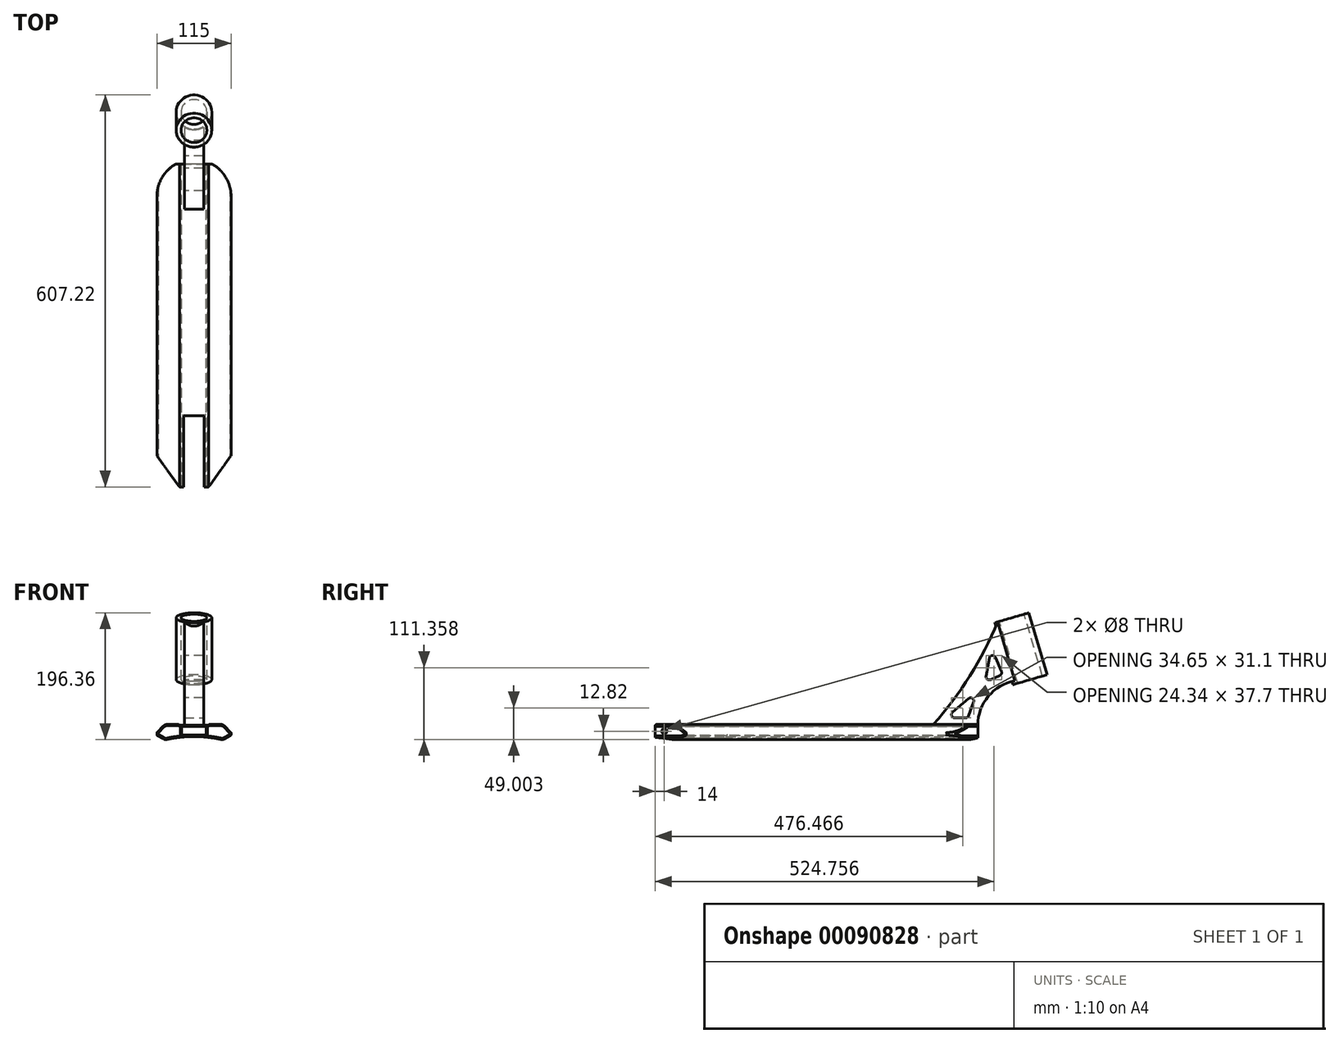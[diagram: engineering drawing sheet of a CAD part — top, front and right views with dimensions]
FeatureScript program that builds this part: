
annotation { "Feature Type Name" : "Feature", "Feature Type Description" : "" }
export const myFeature = defineFeature(function(context is Context, id is Id, definition is map)
    precondition{}
    {
        {
            var Q0;
            Q0=qCreatedBy(makeId("Front.planeOp"),FACE);
            var sketch = newSketch(context, id + "F0", { "sketchPlane" : qUnion([Q0])});
            skLineSegment(sketch, "E0", {"start": v(0, 0) * mm, "end": v(0, 70.92) * mm, "construction": true});
            skLineSegment(sketch, "E1", {"start": v(45, 12.76) * mm, "end": v(57.5, 19.98) * mm});
            skLineSegment(sketch, "E2", {"start": v(57.5, 19.98) * mm, "end": v(57.5, 23.98) * mm});
            skLineSegment(sketch, "E3", {"start": v(57.5, 23.98) * mm, "end": v(45, 36.76) * mm});
            skLineSegment(sketch, "E4", {"start": v(45, 36.76) * mm, "end": v(22.5, 36.76) * mm});
            skLineSegment(sketch, "E5", {"start": v(22.5, 36.76) * mm, "end": v(22.5, 35.46) * mm});
            skLineSegment(sketch, "E6", {"start": v(22.5, 35.46) * mm, "end": v(0, 35.46) * mm});
            skLineSegment(sketch, "E7.MirrorCS", {"start": v(-57.5, 19.98) * mm, "end": v(-57.5, 23.98) * mm});
            skLineSegment(sketch, "E8.MirrorCS", {"start": v(-22.5, 36.76) * mm, "end": v(-22.5, 35.46) * mm});
            skLineSegment(sketch, "E9.MirrorCS", {"start": v(-57.5, 23.98) * mm, "end": v(-45, 36.76) * mm});
            skLineSegment(sketch, "E10.MirrorCS", {"start": v(-45, 36.76) * mm, "end": v(-22.5, 36.76) * mm});
            skLineSegment(sketch, "E11.MirrorCS", {"start": v(-45, 12.76) * mm, "end": v(-57.5, 19.98) * mm});
            skLineSegment(sketch, "E12.MirrorCS", {"start": v(-22.5, 35.46) * mm, "end": v(0, 35.46) * mm});
            skArc(sketch, "E13", {"start": v(45, 12.76) * mm, "mid": v(0, 17.9) * mm, "end": v(-45, 12.76) * mm});
            skSolve(sketch);
        }
        {
            var Q0;
            Q0 = qSketchRegion(id + "F0", true);
            extrude(context, id + "F1", {"entities" : qUnion([Q0]), "depth" : 500 * mm});
        }
        {
            var Q0;
            Q0=qCreatedBy(makeId("Front.planeOp"),FACE);
            var sketch = newSketch(context, id + "F2", { "sketchPlane" : qUnion([Q0])});
            skLineSegment(sketch, "E14", {"start": v(0, 0) * mm, "end": v(0, 112.07) * mm, "construction": true});
            skLineSegment(sketch, "E15.bottom", {"start": v(-19, 33.46) * mm, "end": v(19, 33.46) * mm});
            skLineSegment(sketch, "E15.top", {"start": v(-19, 20.46) * mm, "end": v(19, 20.46) * mm});
            skLineSegment(sketch, "E15.left", {"start": v(-19, 33.46) * mm, "end": v(-19, 20.46) * mm});
            skLineSegment(sketch, "E15.right", {"start": v(19, 33.46) * mm, "end": v(19, 20.46) * mm});
            skSolve(sketch);
        }
        {
            var Q0;
            Q0=makeQuery(id+"F2.imprint","IMPRINT",FACE,{"disambiguationData":[TD([[makeQuery(id+"F2.imprint","IMPRINT",EDGE,{"derivedFrom":sQuery(id+"F2.wireOp",EDGE,"E15.bottom")}),-1.0]])]});
            extrude(context, id + "F3", {"entities" : qUnion([Q0]), "operationType" : NewBodyOperationType.REMOVE, "depth" : 500 * mm});
        }
        {
            var Q0;
            Q0=makeQuery(id+"F1.opExtrude","SWEPT_EDGE",EDGE,{"disambiguationData":[OSD([sQuery(id+"F0.wireOp",EDGE,"E4"),sQuery(id+"F0.wireOp",EDGE,"E5")])]});
            var Q1;
            Q1=makeQuery(id+"F1.opExtrude","SWEPT_EDGE",EDGE,{"disambiguationData":[OSD([sQuery(id+"F0.wireOp",EDGE,"E8.MirrorCS"),sQuery(id+"F0.wireOp",EDGE,"E10.MirrorCS")])]});
            fillet(context, id + "F4", {"entities" : qUnion([Q0, Q1]), "radius" : 2 * mm, "tangentPropagation" : true, "allowEdgeOverflow" : false});
        }
        {
            var Q0;
            Q0=makeQuery(id+"F1.opExtrude","SWEPT_EDGE",EDGE,{"disambiguationData":[OSD([sQuery(id+"F0.wireOp",EDGE,"E9.MirrorCS"),sQuery(id+"F0.wireOp",EDGE,"E10.MirrorCS")])]});
            var Q1;
            Q1=makeQuery(id+"F1.opExtrude","SWEPT_EDGE",EDGE,{"disambiguationData":[OSD([sQuery(id+"F0.wireOp",EDGE,"E3"),sQuery(id+"F0.wireOp",EDGE,"E4")])]});
            var Q2;
            Q2=makeQuery(id+"F1.opExtrude","SWEPT_EDGE",EDGE,{"disambiguationData":[OSD([sQuery(id+"F0.wireOp",EDGE,"E1"),sQuery(id+"F0.wireOp",EDGE,"E13")])]});
            var Q3;
            Q3=makeQuery(id+"F1.opExtrude","SWEPT_EDGE",EDGE,{"disambiguationData":[OSD([sQuery(id+"F0.wireOp",EDGE,"E11.MirrorCS"),sQuery(id+"F0.wireOp",EDGE,"E13")])]});
            fillet(context, id + "F5", {"entities" : qUnion([Q0, Q1, Q2, Q3]), "radius" : 9 * mm, "tangentPropagation" : true, "allowEdgeOverflow" : false});
        }
        {
            var Q0;
            Q0=makeQuery(id+"F1.opExtrude","SWEPT_EDGE",EDGE,{"disambiguationData":[OSD([sQuery(id+"F0.wireOp",EDGE,"E2"),sQuery(id+"F0.wireOp",EDGE,"E3")])]});
            var Q1;
            Q1=makeQuery(id+"F1.opExtrude","SWEPT_EDGE",EDGE,{"disambiguationData":[OSD([sQuery(id+"F0.wireOp",EDGE,"E1"),sQuery(id+"F0.wireOp",EDGE,"E2")])]});
            var Q2;
            Q2=makeQuery(id+"F1.opExtrude","SWEPT_EDGE",EDGE,{"disambiguationData":[OSD([sQuery(id+"F0.wireOp",EDGE,"E7.MirrorCS"),sQuery(id+"F0.wireOp",EDGE,"E9.MirrorCS")])]});
            var Q3;
            Q3=makeQuery(id+"F1.opExtrude","SWEPT_EDGE",EDGE,{"disambiguationData":[OSD([sQuery(id+"F0.wireOp",EDGE,"E7.MirrorCS"),sQuery(id+"F0.wireOp",EDGE,"E11.MirrorCS")])]});
            fillet(context, id + "F6", {"entities" : qUnion([Q0, Q1, Q2, Q3]), "radius" : 1 * mm, "tangentPropagation" : true, "allowEdgeOverflow" : false});
        }
        {
            var Q0;
            Q0=makeQuery(id+"F1.opExtrude","CAP_FACE",FACE,{"disambiguationData":[OSD([sQuery(id+"F0.wireOp",EDGE,"E1"),sQuery(id+"F0.wireOp",EDGE,"E2"),sQuery(id+"F0.wireOp",EDGE,"E3"),sQuery(id+"F0.wireOp",EDGE,"E4"),sQuery(id+"F0.wireOp",EDGE,"E5"),sQuery(id+"F0.wireOp",EDGE,"E6"),sQuery(id+"F0.wireOp",EDGE,"E7.MirrorCS"),sQuery(id+"F0.wireOp",EDGE,"E8.MirrorCS"),sQuery(id+"F0.wireOp",EDGE,"E9.MirrorCS"),sQuery(id+"F0.wireOp",EDGE,"E10.MirrorCS"),sQuery(id+"F0.wireOp",EDGE,"E11.MirrorCS"),sQuery(id+"F0.wireOp",EDGE,"E12.MirrorCS"),sQuery(id+"F0.wireOp",EDGE,"E13")])],"isStart":false});
            var sketch = newSketch(context, id + "F7", { "sketchPlane" : qUnion([Q0])});
            skLineSegment(sketch, "E16.0", {"start": v(-57.21, 24.27) * mm, "end": v(-47.65, 34.06) * mm});
            skArc(sketch, "E17.0", {"start": v(-41.21, 36.76) * mm, "mid": v(-44.7, 36.06) * mm, "end": v(-47.65, 34.06) * mm});
            skLineSegment(sketch, "E18.0", {"start": v(-57.5, 20.56) * mm, "end": v(-57.5, 23.57) * mm});
            skArc(sketch, "E19.0", {"start": v(-57.21, 24.27) * mm, "mid": v(-57.43, 23.95) * mm, "end": v(-57.5, 23.57) * mm});
            skArc(sketch, "E20.0", {"start": v(-57.5, 20.56) * mm, "mid": v(-57.37, 20.06) * mm, "end": v(-57, 19.7) * mm});
            skLineSegment(sketch, "E21.0", {"start": v(-41.21, 36.76) * mm, "end": v(-24.37, 36.76) * mm});
            skArc(sketch, "E22.0", {"start": v(57.5, 23.57) * mm, "mid": v(57.43, 23.95) * mm, "end": v(57.21, 24.27) * mm});
            skArc(sketch, "E23.0", {"start": v(57, 19.7) * mm, "mid": v(57.37, 20.06) * mm, "end": v(57.5, 20.56) * mm});
            skLineSegment(sketch, "E24.0", {"start": v(57.5, 20.56) * mm, "end": v(57.5, 23.57) * mm});
            skLineSegment(sketch, "E25.0", {"start": v(57.21, 24.27) * mm, "end": v(47.65, 34.06) * mm});
            skLineSegment(sketch, "E26.0", {"start": v(48.03, 14.51) * mm, "end": v(57, 19.7) * mm});
            skArc(sketch, "E27.0", {"start": v(41.66, 13.5) * mm, "mid": v(44.94, 13.42) * mm, "end": v(48.03, 14.51) * mm});
            skArc(sketch, "E28.0", {"start": v(41.66, 13.5) * mm, "mid": v(0, 17.9) * mm, "end": v(-41.66, 13.5) * mm});
            skArc(sketch, "E29.0", {"start": v(47.65, 34.06) * mm, "mid": v(44.7, 36.06) * mm, "end": v(41.21, 36.76) * mm});
            skLineSegment(sketch, "E30.0", {"start": v(41.21, 36.76) * mm, "end": v(24.37, 36.76) * mm});
            skLineSegment(sketch, "E31.0", {"start": v(22.5, 35.46) * mm, "end": v(-22.5, 35.46) * mm});
            skLineSegment(sketch, "E32.0", {"start": v(-47.03, 16.25) * mm, "end": v(-55, 20.85) * mm});
            skArc(sketch, "E33.0", {"start": v(-56.89, 20.56) * mm, "mid": v(-56.83, 20.36) * mm, "end": v(-56.7, 20.22) * mm});
            skLineSegment(sketch, "E34.0", {"start": v(-55.5, 21.71) * mm, "end": v(-55.5, 22.76) * mm});
            skLineSegment(sketch, "E35.0", {"start": v(-55.21, 23.46) * mm, "end": v(-46.22, 32.66) * mm});
            skPoint(sketch, "E36.visualSharp", {"position": v(-55.5, 23.16) * mm});
            skArc(sketch, "E36.filletArc", {"start": v(-55.21, 23.46) * mm, "mid": v(-55.43, 23.13) * mm, "end": v(-55.5, 22.76) * mm});
            skPoint(sketch, "E37.visualSharp", {"position": v(-55.5, 21.13) * mm});
            skArc(sketch, "E37.filletArc", {"start": v(-55.5, 21.71) * mm, "mid": v(-55.37, 21.21) * mm, "end": v(-55, 20.85) * mm});
            skArc(sketch, "E38.0", {"start": v(-41.21, 34.76) * mm, "mid": v(-43.93, 34.22) * mm, "end": v(-46.22, 32.66) * mm});
            skArc(sketch, "E39.0", {"start": v(-47.03, 16.25) * mm, "mid": v(-44.63, 15.4) * mm, "end": v(-42.07, 15.46) * mm});
            skArc(sketch, "E40.0", {"start": v(42.07, 15.46) * mm, "mid": v(31.58, 17.4) * mm, "end": v(21, 18.8) * mm});
            skArc(sketch, "E41.0", {"start": v(42.07, 15.46) * mm, "mid": v(44.63, 15.4) * mm, "end": v(47.03, 16.25) * mm});
            skLineSegment(sketch, "E42.0", {"start": v(47.03, 16.25) * mm, "end": v(55, 20.85) * mm});
            skLineSegment(sketch, "E43.0", {"start": v(55.21, 23.46) * mm, "end": v(46.22, 32.66) * mm});
            skLineSegment(sketch, "E44.0", {"start": v(55.5, 21.71) * mm, "end": v(55.5, 22.76) * mm});
            skPoint(sketch, "E45.visualSharp", {"position": v(55.5, 21.13) * mm});
            skArc(sketch, "E45.filletArc", {"start": v(55, 20.85) * mm, "mid": v(55.37, 21.21) * mm, "end": v(55.5, 21.71) * mm});
            skPoint(sketch, "E46.visualSharp", {"position": v(55.5, 23.16) * mm});
            skArc(sketch, "E46.filletArc", {"start": v(55.5, 22.76) * mm, "mid": v(55.43, 23.13) * mm, "end": v(55.21, 23.46) * mm});
            skArc(sketch, "E47.0", {"start": v(46.22, 32.66) * mm, "mid": v(43.93, 34.22) * mm, "end": v(41.21, 34.76) * mm});
            skLineSegment(sketch, "E48", {"start": v(-21, 33.46) * mm, "end": v(-22.5, 33.46) * mm});
            skLineSegment(sketch, "E49", {"start": v(-41.21, 34.76) * mm, "end": v(-24.37, 34.76) * mm});
            skArc(sketch, "E50", {"start": v(-22.5, 33.46) * mm, "mid": v(-23.23, 34.4) * mm, "end": v(-24.37, 34.76) * mm});
            skLineSegment(sketch, "E51", {"start": v(-21, 33.46) * mm, "end": v(-21, 18.8) * mm});
            skLineSegment(sketch, "E52.0", {"start": v(41.21, 34.76) * mm, "end": v(24.37, 34.76) * mm});
            skLineSegment(sketch, "E53", {"start": v(21, 33.46) * mm, "end": v(22.5, 33.46) * mm});
            skArc(sketch, "E54", {"start": v(24.37, 34.76) * mm, "mid": v(23.23, 34.4) * mm, "end": v(22.5, 33.46) * mm});
            skLineSegment(sketch, "E55", {"start": v(21, 33.46) * mm, "end": v(21, 18.8) * mm});
            skArc(sketch, "E56.trimOffspring", {"start": v(-21, 18.8) * mm, "mid": v(-31.58, 17.4) * mm, "end": v(-42.07, 15.46) * mm});
            skSolve(sketch);
        }
        {
            var Q0;
            Q0=makeQuery(id+"F7.imprint","IMPRINT",FACE,{"disambiguationData":[TD([[makeQuery(id+"F7.imprint","IMPRINT",EDGE,{"derivedFrom":sQuery(id+"F7.wireOp",EDGE,"E40.0")}),-1.0]])]});
            var Q1;
            Q1=makeQuery(id+"F7.imprint","IMPRINT",FACE,{"disambiguationData":[TD([[makeQuery(id+"F7.imprint","IMPRINT",EDGE,{"derivedFrom":sQuery(id+"F7.wireOp",EDGE,"E32.0")}),-1.0]])]});
            extrude(context, id + "F8", {"entities" : qUnion([Q0, Q1]), "operationType" : NewBodyOperationType.REMOVE, "oppositeDirection" : true, "depth" : 500 * mm});
        }
        {
            var Q0;
            Q0=qCreatedBy(makeId("Top.planeOp"),FACE);
            var sketch = newSketch(context, id + "F9", { "sketchPlane" : qUnion([Q0])});
            skArc(sketch, "E57", {"start": v(57.5, -50) * mm, "mid": v(0, 7.5) * mm, "end": v(-57.5, -50) * mm});
            skLineSegment(sketch, "E58", {"start": v(-57.5, -50) * mm, "end": v(-57.5, 30) * mm});
            skLineSegment(sketch, "E59", {"start": v(57.5, -50) * mm, "end": v(57.5, 30) * mm});
            skLineSegment(sketch, "E60", {"start": v(57.5, 30) * mm, "end": v(-57.5, 30) * mm});
            skSolve(sketch);
        }
        {
            var Q0;
            Q0 = qSketchRegion(id + "F9", true);
            extrude(context, id + "F10", {"entities" : qUnion([Q0]), "operationType" : NewBodyOperationType.REMOVE, "depth" : 174.35 * mm});
        }
        {
            var Q0;
            Q0=qCreatedBy(makeId("Top.planeOp"),FACE);
            var sketch = newSketch(context, id + "F11", { "sketchPlane" : qUnion([Q0])});
            skLineSegment(sketch, "E61", {"start": v(57.21, -543.3) * mm, "end": v(57.21, -443.3) * mm});
            skLineSegment(sketch, "E62", {"start": v(39.1, -500) * mm, "end": v(16, -500) * mm});
            skLineSegment(sketch, "E63", {"start": v(16, -500) * mm, "end": v(16, -390) * mm});
            skLineSegment(sketch, "E64", {"start": v(16, -390) * mm, "end": v(-16, -390) * mm});
            skLineSegment(sketch, "E65", {"start": v(-16, -390) * mm, "end": v(-16, -500) * mm});
            skLineSegment(sketch, "E66", {"start": v(-16, -500) * mm, "end": v(-34.18, -500) * mm});
            skLineSegment(sketch, "E67", {"start": v(-57.21, -443.3) * mm, "end": v(-57.21, -543.3) * mm});
            skLineSegment(sketch, "E68", {"start": v(-57.21, -543.3) * mm, "end": v(57.21, -543.3) * mm});
            skLineSegment(sketch, "E69", {"start": v(57.21, -506.22) * mm, "end": v(68, -506.22) * mm});
            skLineSegment(sketch, "E70", {"start": v(68, -506.22) * mm, "end": v(68, -452.22) * mm});
            skLineSegment(sketch, "E71", {"start": v(68, -452.22) * mm, "end": v(57.21, -452.22) * mm});
            skLineSegment(sketch, "E72", {"start": v(57.21, -452.22) * mm, "end": v(57.21, -506.22) * mm});
            skLineSegment(sketch, "E73", {"start": v(-57.21, -506.22) * mm, "end": v(-68, -506.22) * mm});
            skLineSegment(sketch, "E74", {"start": v(-68, -506.22) * mm, "end": v(-68, -452.22) * mm});
            skLineSegment(sketch, "E75", {"start": v(-68, -452.22) * mm, "end": v(-57.21, -452.22) * mm});
            skLineSegment(sketch, "E76", {"start": v(-57.21, -452.22) * mm, "end": v(-57.21, -506.22) * mm});
            skLineSegment(sketch, "E77.0", {"start": v(22.5, -500) * mm, "end": v(22.5, 0) * mm});
            skLineSegment(sketch, "E78.0", {"start": v(-22.5, -500) * mm, "end": v(-22.5, 0) * mm});
            skLineSegment(sketch, "E79", {"start": v(57.21, -452.22) * mm, "end": v(22.5, -500) * mm});
            skLineSegment(sketch, "E80", {"start": v(-57.21, -452.22) * mm, "end": v(-22.5, -500) * mm});
            skSolve(sketch);
        }
        {
            var Q0;
            Q0 = qSketchRegion(id + "F11", true);
            extrude(context, id + "F12", {"entities" : qUnion([Q0]), "operationType" : NewBodyOperationType.REMOVE, "depth" : 74.4 * mm});
        }
        {
            var Q0;
            Q0=qCreatedBy(makeId("Right.planeOp"),FACE);
            var sketch = newSketch(context, id + "F13", { "sketchPlane" : qUnion([Q0])});
            skLineSegment(sketch, "E81", {"start": v(0, 35.46) * mm, "end": v(-70, 35.46) * mm});
            skArc(sketch, "E82", {"start": v(-70, 35.46) * mm, "mid": v(-12.76, 111.1) * mm, "end": v(30.63, 195.46) * mm});
            skLineSegment(sketch, "E83", {"start": v(58.76, 99.5) * mm, "end": v(58.3, 104.48) * mm});
            skArc(sketch, "E84", {"start": v(58.3, 104.48) * mm, "mid": v(16.53, 80.64) * mm, "end": v(0, 35.46) * mm});
            skLineSegment(sketch, "E85", {"start": v(30.63, 195.46) * mm, "end": v(74.78, 208.4) * mm});
            skLineSegment(sketch, "E86", {"start": v(74.78, 208.4) * mm, "end": v(102.9, 112.44) * mm});
            skLineSegment(sketch, "E87", {"start": v(58.76, 99.5) * mm, "end": v(102.9, 112.44) * mm});
            skPoint(sketch, "E88.orphan", {"position": v(106.7, 99.5) * mm});
            skSolve(sketch);
        }
        {
            var Q0;
            Q0=makeQuery(id+"F13.imprint","IMPRINT",FACE,{"disambiguationData":[TD([[makeQuery(id+"F13.imprint","IMPRINT",EDGE,{"derivedFrom":sQuery(id+"F13.wireOp",EDGE,"E81")}),-1.0]])]});
            extrude(context, id + "F14", {"entities" : qUnion([Q0]), "operationType" : NewBodyOperationType.ADD, "endBound" : BoundingType.SYMMETRIC, "depth" : 30 * mm});
        }
        {
            var Q0;
            Q0=makeQuery(id+"F14.opExtrude","SWEPT_FACE",FACE,{"disambiguationData":[OSD([sQuery(id+"F13.wireOp",EDGE,"E85")])]});
            var sketch = newSketch(context, id + "F15", { "sketchPlane" : qUnion([Q0])});
            skCircle(sketch, "E89", {"center": v(0, 107.37) * mm, "radius": 27.5 * mm});
            skPoint(sketch, "E89.centerSnap0", {"position": v(15, 107.37) * mm});
            skPoint(sketch, "E89.centerSnap1", {"position": v(0, 130.37) * mm});
            skSolve(sketch);
        }
        {
            var Q0;
            {var subQ0=sQuery(id+"F15.wireOp",EDGE,"E89");var subQ1=makeQuery(id+"F14.opExtrude","SWEPT_EDGE",EDGE,{"disambiguationData":[OSD([sQuery(id+"F13.wireOp",EDGE,"E85"),sQuery(id+"F13.wireOp",EDGE,"E86")])]});var subQ2=makeQuery(id+"F15.imprint","INTERSECT",VERTEX,{"disambiguationData":[OD(0.0)],"derivedFrom":[subQ1,subQ0]});Q0=makeQuery(id+"F15.imprint","IMPRINT",FACE,{"disambiguationData":[TD([[makeQuery(id+"F15.imprint","IMPRINT",EDGE,{"disambiguationData":[TD([[subQ2,-1.0]])],"derivedFrom":subQ0}),1.0]])]});}
            var Q1;
            {var subQ0=sQuery(id+"F15.wireOp",EDGE,"E89");var subQ1=makeQuery(id+"F14.opExtrude","CAP_EDGE",EDGE,{"disambiguationData":[OSD([sQuery(id+"F13.wireOp",EDGE,"E85")])],"isStart":false});var subQ2=makeQuery(id+"F15.imprint","INTERSECT",VERTEX,{"disambiguationData":[OD(0.0)],"derivedFrom":[subQ1,subQ0]});Q1=makeQuery(id+"F15.imprint","IMPRINT",FACE,{"disambiguationData":[TD([[makeQuery(id+"F15.imprint","IMPRINT",EDGE,{"disambiguationData":[TD([[subQ2,1.0]])],"derivedFrom":subQ0}),1.0]])]});}
            var Q2;
            {var subQ0=sQuery(id+"F15.wireOp",EDGE,"E89");var subQ1=makeQuery(id+"F14.opExtrude","CAP_EDGE",EDGE,{"disambiguationData":[OSD([sQuery(id+"F13.wireOp",EDGE,"E85")])],"isStart":true});var subQ2=makeQuery(id+"F15.imprint","INTERSECT",VERTEX,{"disambiguationData":[OD(0.0)],"derivedFrom":[subQ1,subQ0]});Q2=makeQuery(id+"F15.imprint","IMPRINT",FACE,{"disambiguationData":[TD([[makeQuery(id+"F15.imprint","IMPRINT",EDGE,{"disambiguationData":[TD([[subQ2,-1.0]])],"derivedFrom":subQ0}),1.0]])]});}
            var Q3;
            {var subQ0=sQuery(id+"F15.wireOp",EDGE,"E89");var subQ1=sQuery(id+"F13.wireOp",EDGE,"E85");var subQ8=makeQuery(id+"F14.opExtrude","CAP_EDGE",EDGE,{"disambiguationData":[OSD([subQ1])],"isStart":true});var subQ9=makeQuery(id+"F15.imprint","INTERSECT",VERTEX,{"disambiguationData":[OD(0.0)],"derivedFrom":[subQ8,subQ0]});Q3=makeQuery(id+"F15.imprint","IMPRINT",FACE,{"disambiguationData":[TD([[makeQuery(id+"F15.imprint","IMPRINT",EDGE,{"disambiguationData":[TD([[subQ9,1.0]])],"derivedFrom":subQ8}),-1.0]])]});}
            var Q4;
            {var subQ0=sQuery(id+"F15.wireOp",EDGE,"E89");var subQ1=makeQuery(id+"F14.opExtrude","SWEPT_EDGE",EDGE,{"disambiguationData":[OSD([sQuery(id+"F13.wireOp",EDGE,"E82"),sQuery(id+"F13.wireOp",EDGE,"E85")])]});var subQ2=makeQuery(id+"F15.imprint","INTERSECT",VERTEX,{"disambiguationData":[OD(0.0)],"derivedFrom":[subQ1,subQ0]});Q4=makeQuery(id+"F15.imprint","IMPRINT",FACE,{"disambiguationData":[TD([[makeQuery(id+"F15.imprint","IMPRINT",EDGE,{"disambiguationData":[TD([[subQ2,-1.0]])],"derivedFrom":subQ0}),1.0]])]});}
            var Q5;
            Q5=makeQuery(id+"F14.opExtrude","SWEPT_FACE",FACE,{"disambiguationData":[OSD([sQuery(id+"F13.wireOp",EDGE,"E87")])]});
            extrude(context, id + "F16", {"entities" : qUnion([Q0, Q1, Q2, Q3, Q4]), "operationType" : NewBodyOperationType.ADD, "endBound" : BoundingType.UP_TO_SURFACE, "oppositeDirection" : true, "endBoundEntityFace" : qUnion([Q5]), "depth" : 125.58 * mm});
        }
        {
            var Q0;
            Q0=sQuery(id+"F15.wireOp",VERTEX,"E89.center");
            var Q1;
            Q1=makeQuery(id+"F1.opExtrude","SWEPT_BODY",BODY,{"disambiguationData":[OSD([sQuery(id+"F0.wireOp",EDGE,"E1"),sQuery(id+"F0.wireOp",EDGE,"E2"),sQuery(id+"F0.wireOp",EDGE,"E3"),sQuery(id+"F0.wireOp",EDGE,"E4"),sQuery(id+"F0.wireOp",EDGE,"E5"),sQuery(id+"F0.wireOp",EDGE,"E6"),sQuery(id+"F0.wireOp",EDGE,"E7.MirrorCS"),sQuery(id+"F0.wireOp",EDGE,"E8.MirrorCS"),sQuery(id+"F0.wireOp",EDGE,"E9.MirrorCS"),sQuery(id+"F0.wireOp",EDGE,"E10.MirrorCS"),sQuery(id+"F0.wireOp",EDGE,"E11.MirrorCS"),sQuery(id+"F0.wireOp",EDGE,"E12.MirrorCS"),sQuery(id+"F0.wireOp",EDGE,"E13")])]});
            hole(context, id + "F17", {"style" : HoleStyle.SIMPLE, "endStyle" : HoleEndStyle.THROUGH, "holeDiameter" : 40 * mm, "locations" : qUnion([Q0]), "scope" : qUnion([Q1]), "isTappedThrough" : true});
        }
        {
            var Q0;
            Q0=makeQuery(id+"F8.boolean.opBoolean","COPY",FACE,{"derivedFrom":makeQuery(id+"F8.opExtrude","SWEPT_FACE",FACE,{"disambiguationData":[OSD([sQuery(id+"F7.wireOp",EDGE,"E55")])]})});
            var sketch = newSketch(context, id + "F18", { "sketchPlane" : qUnion([Q0])});
            skPoint(sketch, "E90", {"position": v(-486, 26.13) * mm});
            skPoint(sketch, "E90.positionSnap0", {"position": v(-500, 26.13) * mm});
            skSolve(sketch);
        }
        {
            var Q0;
            Q0=sQuery(id+"F18.wireOp",VERTEX,"E90");
            var Q1;
            Q1=makeQuery(id+"F1.opExtrude","SWEPT_BODY",BODY,{"disambiguationData":[OSD([sQuery(id+"F0.wireOp",EDGE,"E1"),sQuery(id+"F0.wireOp",EDGE,"E2"),sQuery(id+"F0.wireOp",EDGE,"E3"),sQuery(id+"F0.wireOp",EDGE,"E4"),sQuery(id+"F0.wireOp",EDGE,"E5"),sQuery(id+"F0.wireOp",EDGE,"E6"),sQuery(id+"F0.wireOp",EDGE,"E7.MirrorCS"),sQuery(id+"F0.wireOp",EDGE,"E8.MirrorCS"),sQuery(id+"F0.wireOp",EDGE,"E9.MirrorCS"),sQuery(id+"F0.wireOp",EDGE,"E10.MirrorCS"),sQuery(id+"F0.wireOp",EDGE,"E11.MirrorCS"),sQuery(id+"F0.wireOp",EDGE,"E12.MirrorCS"),sQuery(id+"F0.wireOp",EDGE,"E13")])]});
            hole(context, id + "F19", {"style" : HoleStyle.SIMPLE, "endStyle" : HoleEndStyle.THROUGH, "holeDiameter" : 8 * mm, "locations" : qUnion([Q0]), "scope" : qUnion([Q1]), "isTappedThrough" : true});
        }
        {
            var Q0;
            Q0=makeQuery(id+"F14.opExtrude","CAP_FACE",FACE,{"disambiguationData":[OSD([sQuery(id+"F13.wireOp",EDGE,"E81"),sQuery(id+"F13.wireOp",EDGE,"E82"),sQuery(id+"F13.wireOp",EDGE,"E83"),sQuery(id+"F13.wireOp",EDGE,"E84"),sQuery(id+"F13.wireOp",EDGE,"E85"),sQuery(id+"F13.wireOp",EDGE,"E86"),sQuery(id+"F13.wireOp",EDGE,"E87")])],"isStart":false});
            var sketch = newSketch(context, id + "F20", { "sketchPlane" : qUnion([Q0])});
            skLineSegment(sketch, "E91", {"start": v(-49.4, 46.76) * mm, "end": v(-15.4, 46.76) * mm});
            skLineSegment(sketch, "E92", {"start": v(-15.4, 46.76) * mm, "end": v(0, 89.05) * mm});
            skLineSegment(sketch, "E93", {"start": v(0, 89.05) * mm, "end": v(-49.4, 46.76) * mm});
            skLineSegment(sketch, "E94", {"start": v(20.6, 155.7) * mm, "end": v(10.98, 102.47) * mm});
            skLineSegment(sketch, "E95", {"start": v(10.98, 102.47) * mm, "end": v(38.5, 114.4) * mm});
            skLineSegment(sketch, "E96", {"start": v(38.5, 114.4) * mm, "end": v(20.6, 155.7) * mm});
            skSolve(sketch);
        }
        {
            var Q0;
            Q0 = qSketchRegion(id + "F20", true);
            extrude(context, id + "F21", {"entities" : qUnion([Q0]), "operationType" : NewBodyOperationType.REMOVE, "oppositeDirection" : true, "depth" : 55 * mm});
        }
        {
            var Q0;
            Q0=makeQuery(id+"F21.boolean.opBoolean","COPY",EDGE,{"derivedFrom":makeQuery(id+"F21.opExtrude","SWEPT_EDGE",EDGE,{"disambiguationData":[OSD([sQuery(id+"F20.wireOp",EDGE,"E95"),sQuery(id+"F20.wireOp",EDGE,"E96")])]})});
            var Q1;
            Q1=makeQuery(id+"F21.boolean.opBoolean","COPY",EDGE,{"derivedFrom":makeQuery(id+"F21.opExtrude","SWEPT_EDGE",EDGE,{"disambiguationData":[OSD([sQuery(id+"F20.wireOp",EDGE,"E94"),sQuery(id+"F20.wireOp",EDGE,"E95")])]})});
            var Q2;
            Q2=makeQuery(id+"F21.boolean.opBoolean","COPY",EDGE,{"derivedFrom":makeQuery(id+"F21.opExtrude","SWEPT_EDGE",EDGE,{"disambiguationData":[OSD([sQuery(id+"F20.wireOp",EDGE,"E91"),sQuery(id+"F20.wireOp",EDGE,"E93")])]})});
            var Q3;
            Q3=makeQuery(id+"F21.boolean.opBoolean","COPY",EDGE,{"derivedFrom":makeQuery(id+"F21.opExtrude","SWEPT_EDGE",EDGE,{"disambiguationData":[OSD([sQuery(id+"F20.wireOp",EDGE,"E91"),sQuery(id+"F20.wireOp",EDGE,"E92")])]})});
            var Q4;
            Q4=makeQuery(id+"F21.boolean.opBoolean","COPY",EDGE,{"derivedFrom":makeQuery(id+"F21.opExtrude","SWEPT_EDGE",EDGE,{"disambiguationData":[OSD([sQuery(id+"F20.wireOp",EDGE,"E94"),sQuery(id+"F20.wireOp",EDGE,"E96")])]})});
            var Q5;
            Q5=makeQuery(id+"F21.boolean.opBoolean","COPY",EDGE,{"derivedFrom":makeQuery(id+"F21.opExtrude","SWEPT_EDGE",EDGE,{"disambiguationData":[OSD([sQuery(id+"F20.wireOp",EDGE,"E92"),sQuery(id+"F20.wireOp",EDGE,"E93")])]})});
            fillet(context, id + "F22", {"entities" : qUnion([Q0, Q1, Q2, Q3, Q4, Q5]), "radius" : 5 * mm, "tangentPropagation" : true, "allowEdgeOverflow" : false});
        }
        {
            var Q0;
            Q0=makeQuery(id+"F12.boolean.opBoolean","INTERSECT",EDGE,{"derivedFrom":[makeQuery(id+"F3.boolean.opBoolean","COPY",FACE,{"derivedFrom":makeQuery(id+"F3.opExtrude","SWEPT_FACE",FACE,{"disambiguationData":[OSD([sQuery(id+"F2.wireOp",EDGE,"E15.top")])]})}),makeQuery(id+"F12.opExtrude","SWEPT_FACE",FACE,{"disambiguationData":[OSD([sQuery(id+"F11.wireOp",EDGE,"E64")])]})]});
            var Q1;
            Q1=makeQuery(id+"F12.boolean.opBoolean","INTERSECT",EDGE,{"derivedFrom":[makeQuery(id+"F3.boolean.opBoolean","COPY",FACE,{"derivedFrom":makeQuery(id+"F3.opExtrude","SWEPT_FACE",FACE,{"disambiguationData":[OSD([sQuery(id+"F2.wireOp",EDGE,"E15.top")])]})}),makeQuery(id+"F12.opExtrude","SWEPT_FACE",FACE,{"disambiguationData":[OSD([sQuery(id+"F11.wireOp",EDGE,"E63")])]})]});
            var Q2;
            Q2=makeQuery(id+"F12.boolean.opBoolean","INTERSECT",EDGE,{"derivedFrom":[makeQuery(id+"F3.boolean.opBoolean","COPY",FACE,{"derivedFrom":makeQuery(id+"F3.opExtrude","SWEPT_FACE",FACE,{"disambiguationData":[OSD([sQuery(id+"F2.wireOp",EDGE,"E15.top")])]})}),makeQuery(id+"F12.opExtrude","SWEPT_FACE",FACE,{"disambiguationData":[OSD([sQuery(id+"F11.wireOp",EDGE,"E65")])]})]});
            var Q3;
            Q3=makeQuery(id+"F12.boolean.opBoolean","INTERSECT",EDGE,{"derivedFrom":[makeQuery(id+"F3.boolean.opBoolean","COPY",FACE,{"derivedFrom":makeQuery(id+"F3.opExtrude","SWEPT_FACE",FACE,{"disambiguationData":[OSD([sQuery(id+"F2.wireOp",EDGE,"E15.bottom")])]})}),makeQuery(id+"F12.opExtrude","SWEPT_FACE",FACE,{"disambiguationData":[OSD([sQuery(id+"F11.wireOp",EDGE,"E65")])]})]});
            var Q4;
            Q4=makeQuery(id+"F12.boolean.opBoolean","INTERSECT",EDGE,{"derivedFrom":[makeQuery(id+"F3.boolean.opBoolean","COPY",FACE,{"derivedFrom":makeQuery(id+"F3.opExtrude","SWEPT_FACE",FACE,{"disambiguationData":[OSD([sQuery(id+"F2.wireOp",EDGE,"E15.bottom")])]})}),makeQuery(id+"F12.opExtrude","SWEPT_FACE",FACE,{"disambiguationData":[OSD([sQuery(id+"F11.wireOp",EDGE,"E64")])]})]});
            var Q5;
            Q5=makeQuery(id+"F12.boolean.opBoolean","INTERSECT",EDGE,{"derivedFrom":[makeQuery(id+"F3.boolean.opBoolean","COPY",FACE,{"derivedFrom":makeQuery(id+"F3.opExtrude","SWEPT_FACE",FACE,{"disambiguationData":[OSD([sQuery(id+"F2.wireOp",EDGE,"E15.bottom")])]})}),makeQuery(id+"F12.opExtrude","SWEPT_FACE",FACE,{"disambiguationData":[OSD([sQuery(id+"F11.wireOp",EDGE,"E63")])]})]});
            fillet(context, id + "F23", {"entities" : qUnion([Q0, Q1, Q2, Q3, Q4, Q5]), "radius" : 2 * mm, "tangentPropagation" : true, "allowEdgeOverflow" : false});
        }
    });
